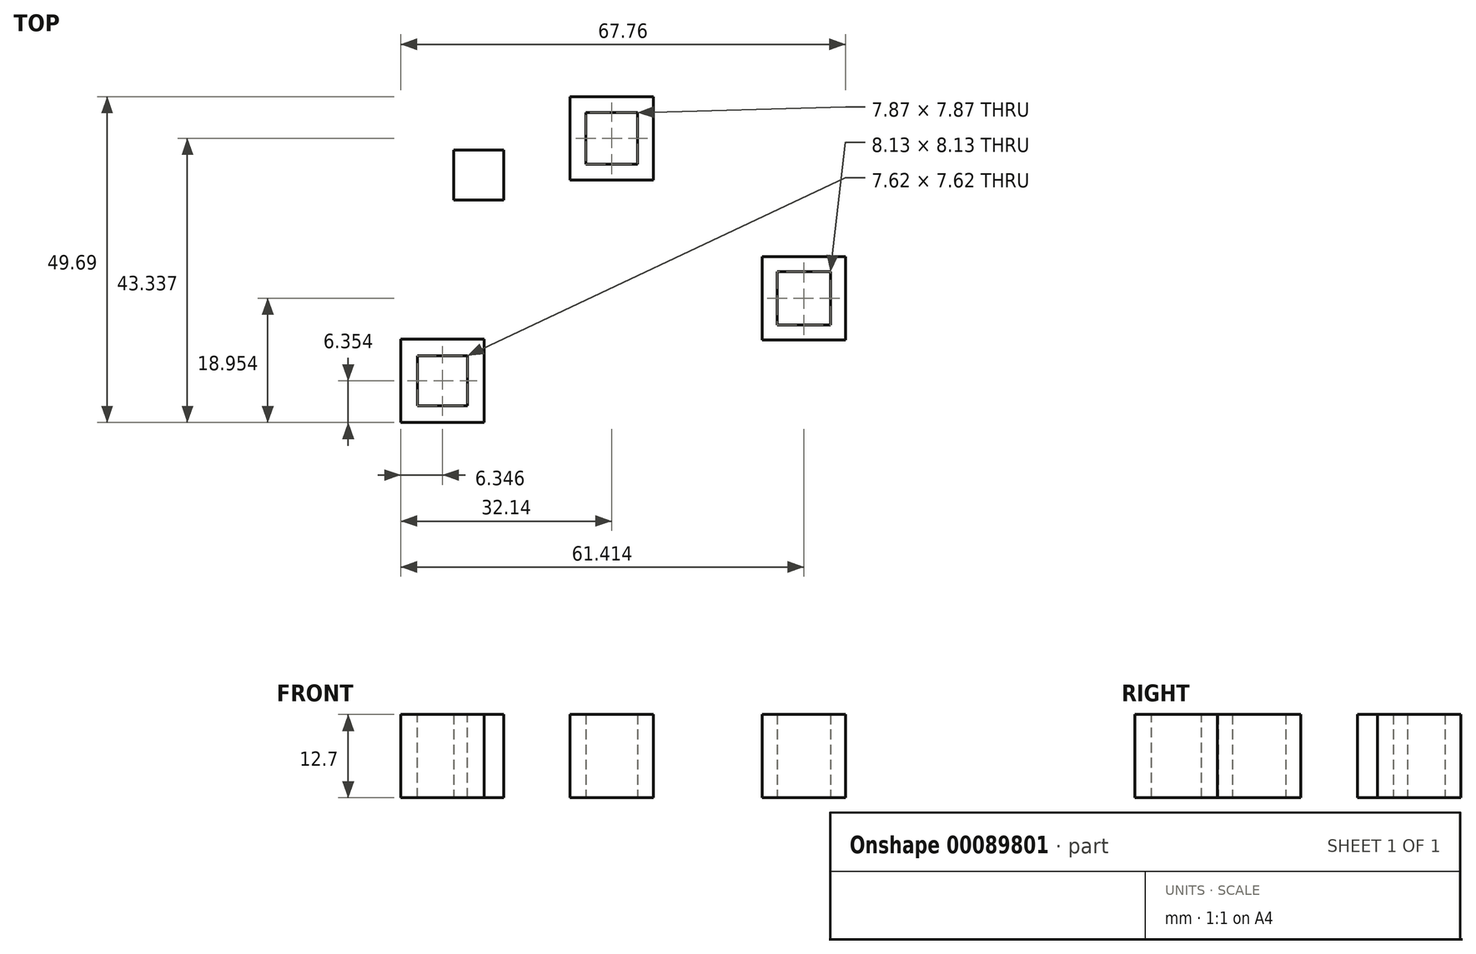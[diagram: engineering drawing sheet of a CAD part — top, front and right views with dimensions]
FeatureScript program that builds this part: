
annotation { "Feature Type Name" : "Feature", "Feature Type Description" : "" }
export const myFeature = defineFeature(function(context is Context, id is Id, definition is map)
    precondition{}
    {
        {
            var Q0;
            Q0=qCreatedBy(makeId("Top.planeOp"),FACE);
            var sketch = newSketch(context, id + "F0", { "sketchPlane" : qUnion([Q0])});
            skLineSegment(sketch, "E0.bottom", {"start": v(-38.5, -22.43) * mm, "end": v(-25.8, -22.43) * mm});
            skLineSegment(sketch, "E0.top", {"start": v(-38.5, -9.73) * mm, "end": v(-25.8, -9.73) * mm});
            skLineSegment(sketch, "E0.left", {"start": v(-38.5, -22.43) * mm, "end": v(-38.5, -9.73) * mm});
            skLineSegment(sketch, "E0.right", {"start": v(-25.8, -22.43) * mm, "end": v(-25.8, -9.73) * mm});
            skSolve(sketch);
        }
        {
            var Q0;
            Q0 = qSketchRegion(id + "F0", true);
            extrude(context, id + "F1", {"entities" : qUnion([Q0]), "depth" : 12.7 * mm});
        }
        {
            var Q0;
            Q0=makeQuery(id+"F1.opExtrude","CAP_FACE",FACE,{"disambiguationData":[OSD([sQuery(id+"F0.wireOp",EDGE,"E0.bottom"),sQuery(id+"F0.wireOp",EDGE,"E0.top"),sQuery(id+"F0.wireOp",EDGE,"E0.left"),sQuery(id+"F0.wireOp",EDGE,"E0.right")])],"isStart":false});
            var sketch = newSketch(context, id + "F2", { "sketchPlane" : qUnion([Q0])});
            skLineSegment(sketch, "E1", {"start": v(-32.14, -9.73) * mm, "end": v(-32.14, -12.27) * mm});
            skLineSegment(sketch, "E2", {"start": v(-25.8, -16.08) * mm, "end": v(-28.33, -16.08) * mm});
            skLineSegment(sketch, "E3", {"start": v(-32.14, -22.43) * mm, "end": v(-32.14, -19.89) * mm});
            skLineSegment(sketch, "E4", {"start": v(-38.5, -16.08) * mm, "end": v(-35.95, -16.08) * mm});
            skLineSegment(sketch, "E5", {"start": v(-28.33, -16.08) * mm, "end": v(-28.33, -12.27) * mm});
            skLineSegment(sketch, "E6", {"start": v(-28.33, -12.27) * mm, "end": v(-37.4, -12.27) * mm});
            skLineSegment(sketch, "E7", {"start": v(-35.95, -16.08) * mm, "end": v(-35.95, -12.27) * mm});
            skLineSegment(sketch, "E8", {"start": v(-35.95, -16.08) * mm, "end": v(-35.95, -20.86) * mm});
            skLineSegment(sketch, "E9", {"start": v(-32.14, -19.89) * mm, "end": v(-35.95, -19.89) * mm});
            skLineSegment(sketch, "E10", {"start": v(-32.14, -19.89) * mm, "end": v(-26.97, -19.89) * mm});
            skLineSegment(sketch, "E11", {"start": v(-28.33, -16.08) * mm, "end": v(-28.33, -19.89) * mm});
            skSolve(sketch);
        }
        {
            var Q0;
            Q0 = qSketchRegion(id + "F2", true);
            extrude(context, id + "F3", {"entities" : qUnion([Q0]), "operationType" : NewBodyOperationType.REMOVE, "oppositeDirection" : true, "depth" : 25.4 * mm});
        }
        {
            var Q0;
            Q0=qCreatedBy(makeId("Top.planeOp"),FACE);
            var sketch = newSketch(context, id + "F4", { "sketchPlane" : qUnion([Q0])});
            skLineSegment(sketch, "E12.bottom", {"start": v(16.57, -9.83) * mm, "end": v(29.27, -9.83) * mm});
            skLineSegment(sketch, "E12.top", {"start": v(16.57, 2.87) * mm, "end": v(29.27, 2.87) * mm});
            skLineSegment(sketch, "E12.left", {"start": v(16.57, -9.83) * mm, "end": v(16.57, 2.87) * mm});
            skLineSegment(sketch, "E12.right", {"start": v(29.27, -9.83) * mm, "end": v(29.27, 2.87) * mm});
            skLineSegment(sketch, "E13", {"start": v(29.27, -3.48) * mm, "end": v(26.99, -3.48) * mm});
            skLineSegment(sketch, "E14", {"start": v(21.67, 2.87) * mm, "end": v(21.67, 0.59) * mm});
            skLineSegment(sketch, "E15", {"start": v(22.92, -9.83) * mm, "end": v(22.92, -7.54) * mm});
            skLineSegment(sketch, "E16", {"start": v(26.99, -3.48) * mm, "end": v(26.99, 1.05) * mm});
            skLineSegment(sketch, "E17", {"start": v(26.99, -3.48) * mm, "end": v(26.99, -7.8) * mm});
            skLineSegment(sketch, "E18", {"start": v(22.92, -7.54) * mm, "end": v(27.8, -7.54) * mm});
            skLineSegment(sketch, "E19", {"start": v(22.92, -7.54) * mm, "end": v(18.76, -7.54) * mm});
            skLineSegment(sketch, "E20", {"start": v(18.86, -3.48) * mm, "end": v(18.86, -7.54) * mm});
            skLineSegment(sketch, "E21", {"start": v(18.86, -7.54) * mm, "end": v(18.86, 1.06) * mm});
            skLineSegment(sketch, "E22", {"start": v(21.67, 0.59) * mm, "end": v(26.99, 0.59) * mm});
            skLineSegment(sketch, "E23", {"start": v(26.99, 0.59) * mm, "end": v(18.86, 0.59) * mm});
            skPoint(sketch, "E24.start.orphan", {"position": v(16.57, -3.48) * mm});
            skLineSegment(sketch, "E25", {"start": v(18.86, 0.59) * mm, "end": v(16.57, 0.59) * mm});
            skSolve(sketch);
        }
        {
            var Q0;
            Q0 = qSketchRegion(id + "F4", true);
            extrude(context, id + "F5", {"entities" : qUnion([Q0]), "depth" : 12.7 * mm});
        }
        {
            var Q0;
            Q0 = qSketchRegion(id + "F4", true);
            extrude(context, id + "F6", {"entities" : qUnion([Q0]), "operationType" : NewBodyOperationType.ADD, "depth" : 12.7 * mm});
        }
        {
            var Q0;
            Q0=qCreatedBy(makeId("Top.planeOp"),FACE);
            var sketch = newSketch(context, id + "F7", { "sketchPlane" : qUnion([Q0])});
            skLineSegment(sketch, "E26.bottom", {"start": v(-30.41, 19.13) * mm, "end": v(-22.8, 19.13) * mm});
            skLineSegment(sketch, "E26.top", {"start": v(-30.41, 11.5) * mm, "end": v(-22.8, 11.5) * mm});
            skLineSegment(sketch, "E26.left", {"start": v(-30.41, 19.13) * mm, "end": v(-30.41, 11.5) * mm});
            skLineSegment(sketch, "E26.right", {"start": v(-22.8, 19.13) * mm, "end": v(-22.8, 11.5) * mm});
            skSolve(sketch);
        }
        {
            var Q0;
            Q0=makeQuery(id+"F7.imprint","IMPRINT",FACE,{"disambiguationData":[TD([[makeQuery(id+"F7.imprint","IMPRINT",EDGE,{"derivedFrom":sQuery(id+"F7.wireOp",EDGE,"E26.bottom")}),-1.0]])]});
            extrude(context, id + "F8", {"entities" : qUnion([Q0]), "depth" : 12.7 * mm});
        }
        {
            var Q0;
            Q0=qCreatedBy(makeId("Top.planeOp"),FACE);
            var sketch = newSketch(context, id + "F9", { "sketchPlane" : qUnion([Q0])});
            skLineSegment(sketch, "E27.bottom", {"start": v(-12.7, 27.26) * mm, "end": v(0, 27.26) * mm});
            skLineSegment(sketch, "E27.top", {"start": v(-12.7, 14.56) * mm, "end": v(0, 14.56) * mm});
            skLineSegment(sketch, "E27.left", {"start": v(-12.7, 27.26) * mm, "end": v(-12.7, 14.56) * mm});
            skLineSegment(sketch, "E27.right", {"start": v(0, 27.26) * mm, "end": v(0, 14.56) * mm});
            skLineSegment(sketch, "E28", {"start": v(-7.79, 14.56) * mm, "end": v(-7.79, 16.97) * mm});
            skLineSegment(sketch, "E29", {"start": v(0, 22) * mm, "end": v(-2.41, 22) * mm});
            skLineSegment(sketch, "E30", {"start": v(-6.35, 27.26) * mm, "end": v(-6.35, 24.84) * mm});
            skLineSegment(sketch, "E31", {"start": v(-12.7, 23.15) * mm, "end": v(-10.29, 23.15) * mm});
            skLineSegment(sketch, "E32", {"start": v(-6.35, 24.84) * mm, "end": v(-1.4, 24.84) * mm});
            skLineSegment(sketch, "E33", {"start": v(-2.41, 22) * mm, "end": v(-2.41, 24.84) * mm});
            skLineSegment(sketch, "E34", {"start": v(-10.29, 23.15) * mm, "end": v(-10.29, 25.58) * mm});
            skLineSegment(sketch, "E35", {"start": v(-6.35, 24.84) * mm, "end": v(-11.8, 24.84) * mm});
            skLineSegment(sketch, "E36", {"start": v(-10.29, 23.15) * mm, "end": v(-10.29, 16.12) * mm});
            skLineSegment(sketch, "E37", {"start": v(-7.79, 16.97) * mm, "end": v(-10.29, 16.97) * mm});
            skLineSegment(sketch, "E38", {"start": v(-7.79, 16.97) * mm, "end": v(-0.94, 16.97) * mm});
            skLineSegment(sketch, "E39", {"start": v(-2.41, 22) * mm, "end": v(-2.41, 16.97) * mm});
            skSolve(sketch);
        }
        {
            var Q0;
            {var subQ1=sQuery(id+"F9.wireOp",EDGE,"E30");Q0=makeQuery(id+"F9.imprint","IMPRINT",FACE,{"disambiguationData":[TD([[makeQuery(id+"F9.imprint","IMPRINT",EDGE,{"derivedFrom":subQ1}),-1.0]])]});}
            var Q1;
            {var subQ4=sQuery(id+"F9.wireOp",EDGE,"E29");Q1=makeQuery(id+"F9.imprint","IMPRINT",FACE,{"disambiguationData":[TD([[makeQuery(id+"F9.imprint","IMPRINT",EDGE,{"derivedFrom":subQ4}),-1.0]])]});}
            var Q2;
            {var subQ4=sQuery(id+"F9.wireOp",EDGE,"E28");Q2=makeQuery(id+"F9.imprint","IMPRINT",FACE,{"disambiguationData":[TD([[makeQuery(id+"F9.imprint","IMPRINT",EDGE,{"derivedFrom":subQ4}),-1.0]])]});}
            var Q3;
            {var subQ0=sQuery(id+"F9.wireOp",EDGE,"E28");Q3=makeQuery(id+"F9.imprint","IMPRINT",FACE,{"disambiguationData":[TD([[makeQuery(id+"F9.imprint","IMPRINT",EDGE,{"derivedFrom":subQ0}),1.0]])]});}
            extrude(context, id + "F10", {"entities" : qUnion([Q0, Q1, Q2, Q3]), "depth" : 12.7 * mm});
        }
    });
